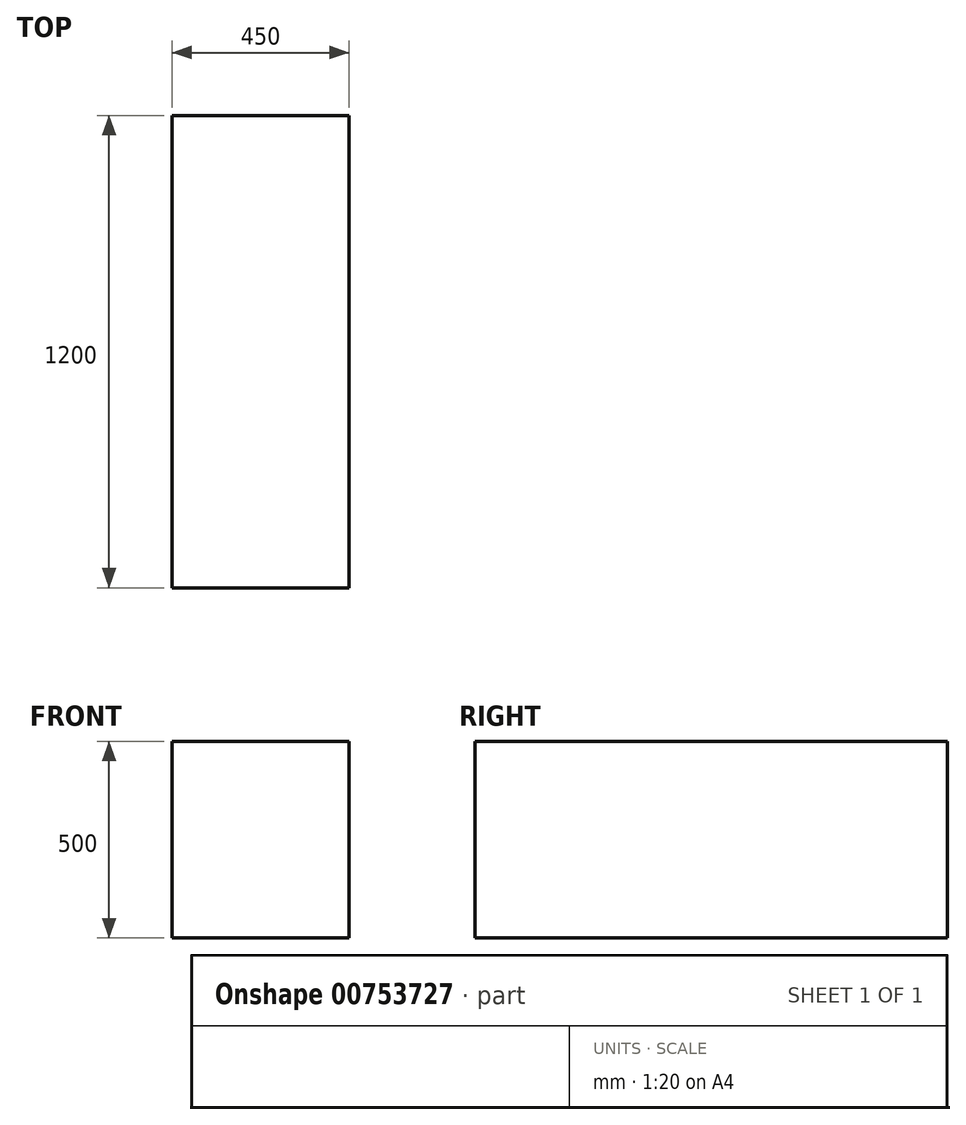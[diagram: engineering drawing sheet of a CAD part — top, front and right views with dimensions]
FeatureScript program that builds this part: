
annotation { "Feature Type Name" : "Feature", "Feature Type Description" : "" }
export const myFeature = defineFeature(function(context is Context, id is Id, definition is map)
    precondition{}
    {
        {
            var Q0;
            Q0=qCreatedBy(makeId("Right.planeOp"),FACE);
            var sketch = newSketch(context, id + "F0", { "sketchPlane" : qUnion([Q0])});
            skLineSegment(sketch, "E0.bottom", {"start": v(-495.48, -271.08) * mm, "end": v(704.52, -271.08) * mm});
            skLineSegment(sketch, "E0.top", {"start": v(-495.48, 228.92) * mm, "end": v(704.52, 228.92) * mm});
            skLineSegment(sketch, "E0.left", {"start": v(-495.48, -271.08) * mm, "end": v(-495.48, 228.92) * mm});
            skLineSegment(sketch, "E0.right", {"start": v(704.52, -271.08) * mm, "end": v(704.52, 228.92) * mm});
            skSolve(sketch);
        }
        {
            var Q0;
            Q0=makeQuery(id+"F0.imprint","IMPRINT",FACE,{"disambiguationData":[TD([[makeQuery(id+"F0.imprint","IMPRINT",EDGE,{"derivedFrom":sQuery(id+"F0.wireOp",EDGE,"E0.bottom")}),1.0]])]});
            extrude(context, id + "F1", {"entities" : qUnion([Q0]), "depth" : 450 * mm, "offsetDistance" : 25 * mm});
        }
    });
